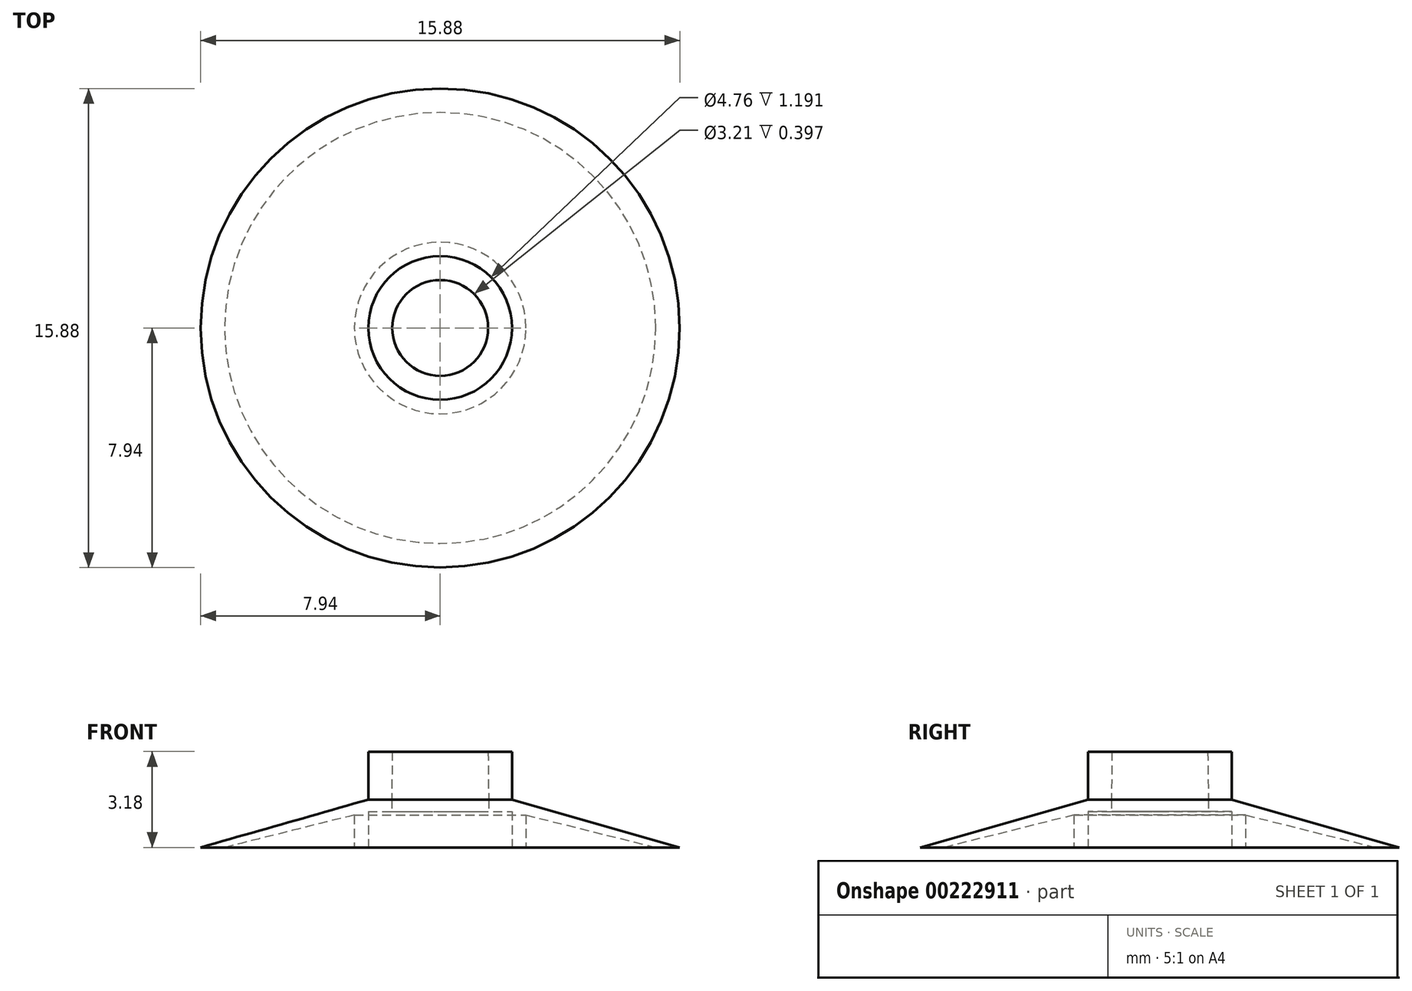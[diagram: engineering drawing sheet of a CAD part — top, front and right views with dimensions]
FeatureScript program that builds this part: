
annotation { "Feature Type Name" : "Feature", "Feature Type Description" : "" }
export const myFeature = defineFeature(function(context is Context, id is Id, definition is map)
    precondition{}
    {
        {
            var Q0;
            Q0=qCreatedBy(makeId("Front.planeOp"),FACE);
            var sketch = newSketch(context, id + "F0", { "sketchPlane" : qUnion([Q0])});
            skLineSegment(sketch, "E0.bottom", {"start": v(0, 0) * mm, "end": v(-2.38, 0) * mm});
            skLineSegment(sketch, "E0.top", {"start": v(0, 1.59) * mm, "end": v(-2.38, 1.59) * mm});
            skLineSegment(sketch, "E0.left", {"start": v(0, 0) * mm, "end": v(0, 1.59) * mm});
            skLineSegment(sketch, "E0.right", {"start": v(-2.38, 0) * mm, "end": v(-2.38, 1.59) * mm});
            skLineSegment(sketch, "E1", {"start": v(0, 1.59) * mm, "end": v(0, 3.17) * mm});
            skLineSegment(sketch, "E2", {"start": v(0, 3.17) * mm, "end": v(-1.59, 3.17) * mm});
            skLineSegment(sketch, "E3", {"start": v(-1.59, 3.17) * mm, "end": v(-1.6, 1.59) * mm});
            skLineSegment(sketch, "E4", {"start": v(-2.38, 1.59) * mm, "end": v(-2.38, 3.17) * mm});
            skLineSegment(sketch, "E5", {"start": v(-2.38, 3.17) * mm, "end": v(-1.59, 3.17) * mm});
            skLineSegment(sketch, "E6", {"start": v(0, 0) * mm, "end": v(-7.94, 0) * mm});
            skLineSegment(sketch, "E7", {"start": v(-7.94, 0) * mm, "end": v(-2.38, 1.59) * mm});
            skPoint(sketch, "E8", {"position": v(-7.14, 0) * mm});
            skLineSegment(sketch, "E9", {"start": v(-7.14, 0) * mm, "end": v(-2.38, 1.2) * mm});
            skLineSegment(sketch, "E10", {"start": v(-2.84, 0) * mm, "end": v(-2.84, 1.07) * mm});
            skLineSegment(sketch, "E11", {"start": v(-2.38, 1.2) * mm, "end": v(-1.6, 1.2) * mm});
            skLineSegment(sketch, "E12", {"start": v(-1.6, 1.2) * mm, "end": v(-1.6, 1.59) * mm});
            skSolve(sketch);
        }
        {
            var Q0;
            {var subQ5=sQuery(id+"F0.wireOp",EDGE,"E10");Q0=makeQuery(id+"F0.imprint","IMPRINT",FACE,{"disambiguationData":[TD([[makeQuery(id+"F0.imprint","IMPRINT",EDGE,{"derivedFrom":subQ5}),-1.0]])]});}
            var Q1;
            {var subQ4=sQuery(id+"F0.wireOp",EDGE,"E7");Q1=makeQuery(id+"F0.imprint","IMPRINT",FACE,{"disambiguationData":[TD([[makeQuery(id+"F0.imprint","IMPRINT",EDGE,{"derivedFrom":subQ4}),-1.0]])]});}
            var Q2;
            {var subQ4=sQuery(id+"F0.wireOp",EDGE,"E11");Q2=makeQuery(id+"F0.imprint","IMPRINT",FACE,{"disambiguationData":[TD([[makeQuery(id+"F0.imprint","IMPRINT",EDGE,{"derivedFrom":subQ4}),1.0]])]});}
            var Q3;
            {var subQ2=sQuery(id+"F0.wireOp",EDGE,"E3");Q3=makeQuery(id+"F0.imprint","IMPRINT",FACE,{"disambiguationData":[TD([[makeQuery(id+"F0.imprint","IMPRINT",EDGE,{"derivedFrom":subQ2}),-1.0]])]});}
            var Q4;
            Q4=sQuery(id+"F0.wireOp",EDGE,"E0.left");
            revolve(context, id + "F1", {"entities" : qUnion([Q0, Q1, Q2, Q3]), "axis" : qUnion([Q4]), "revolveType" : RevolveType.FULL});
        }
    });
